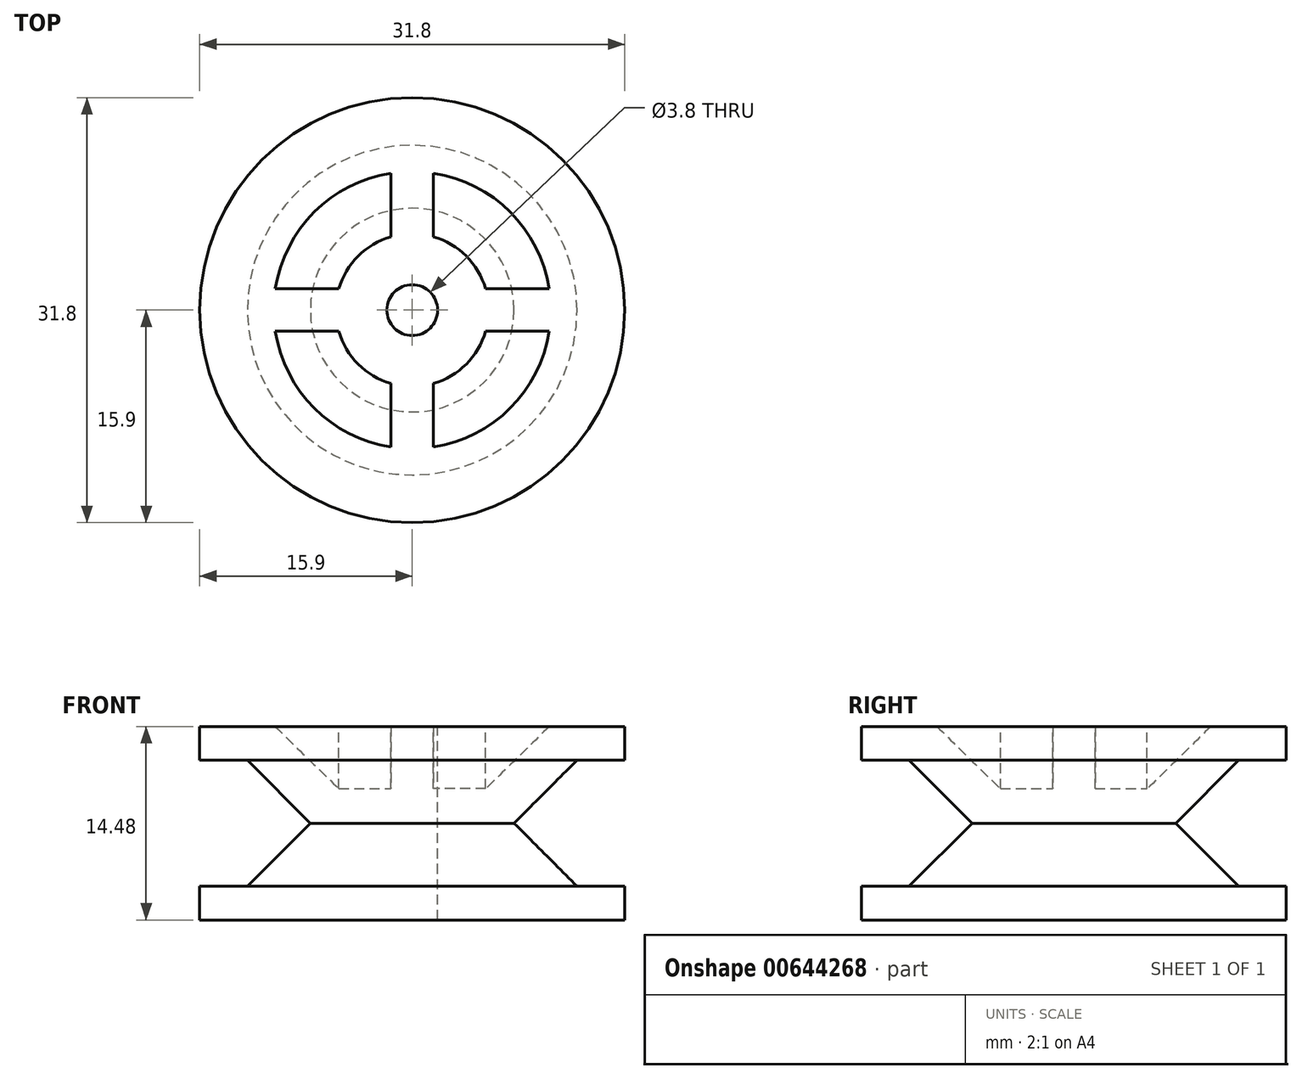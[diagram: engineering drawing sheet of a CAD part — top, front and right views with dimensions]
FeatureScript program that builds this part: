
annotation { "Feature Type Name" : "Feature", "Feature Type Description" : "" }
export const myFeature = defineFeature(function(context is Context, id is Id, definition is map)
    precondition{}
    {
        {
            var Q0;
            Q0=qCreatedBy(makeId("Top.planeOp"),FACE);
            var sketch = newSketch(context, id + "F0", { "sketchPlane" : qUnion([Q0])});
            skCircle(sketch, "E0", {"center": v(0, 0) * mm, "radius": 15.9 * mm});
            skSolve(sketch);
        }
        {
            var Q0;
            Q0 = qSketchRegion(id + "F0", true);
            extrude(context, id + "F1", {"entities" : qUnion([Q0]), "endBound" : BoundingType.SYMMETRIC, "depth" : 14.48 * mm, "offsetDistance" : 25.4 * mm});
        }
        {
            var Q0;
            Q0=makeQuery(id+"F1.opExtrude","CAP_FACE",FACE,{"disambiguationData":[OSD([sQuery(id+"F0.wireOp",EDGE,"E0")])],"isStart":false});
            var sketch = newSketch(context, id + "F2", { "sketchPlane" : qUnion([Q0])});
            skCircle(sketch, "E1", {"center": v(0, 0) * mm, "radius": 1.9 * mm});
            skSolve(sketch);
        }
        {
            var Q0;
            Q0 = qSketchRegion(id + "F2", true);
            extrude(context, id + "F3", {"entities" : qUnion([Q0]), "operationType" : NewBodyOperationType.REMOVE, "endBound" : BoundingType.THROUGH_ALL, "oppositeDirection" : true, "depth" : 25.4 * mm, "offsetDistance" : 25.4 * mm});
        }
        {
            var Q0;
            Q0=qCreatedBy(makeId("Right.planeOp"),FACE);
            var sketch = newSketch(context, id + "F4", { "sketchPlane" : qUnion([Q0])});
            skLineSegment(sketch, "E2", {"start": v(12.33, -4.71) * mm, "end": v(16.18, -4.71) * mm});
            skLineSegment(sketch, "E3", {"start": v(16.18, -4.71) * mm, "end": v(16.18, 4.71) * mm});
            skLineSegment(sketch, "E4", {"start": v(16.18, 4.71) * mm, "end": v(12.33, 4.71) * mm});
            skLineSegment(sketch, "E5", {"start": v(12.33, 4.71) * mm, "end": v(7.62, 0) * mm});
            skLineSegment(sketch, "E6", {"start": v(7.62, 0) * mm, "end": v(12.33, -4.71) * mm});
            skLineSegment(sketch, "E7", {"start": v(0, 0) * mm, "end": v(0, 12.59) * mm, "construction": true});
            skLineSegment(sketch, "E8", {"start": v(5.72, 8.58) * mm, "end": v(5.72, 2.59) * mm});
            skLineSegment(sketch, "E9", {"start": v(5.71, 8.58) * mm, "end": v(11.7, 8.58) * mm});
            skLineSegment(sketch, "E10", {"start": v(11.7, 8.58) * mm, "end": v(5.72, 2.59) * mm});
            skSolve(sketch);
        }
        {
            var Q0;
            Q0 = qSketchRegion(id + "F4", true);
            var Q1;
            Q1=sQuery(id+"F4.wireOp",EDGE,"E7");
            revolve(context, id + "F5", {"operationType" : NewBodyOperationType.REMOVE, "entities" : qUnion([Q0]), "axis" : qUnion([Q1]), "revolveType" : RevolveType.FULL, "oppositeDirection" : true});
        }
        {
            var Q0;
            {var subQ0=sQuery(id+"F0.wireOp",EDGE,"E0");Q0=makeQuery(id+"F5.boolean.opBoolean","SPLIT",FACE,{"disambiguationData":[TD([makeQuery(id+"F1.opExtrude","SWEPT_FACE",FACE,{"disambiguationData":[OSD([subQ0])]})])],"derivedFrom":makeQuery(id+"F1.opExtrude","CAP_FACE",FACE,{"disambiguationData":[OSD([subQ0])],"isStart":false})});}
            var sketch = newSketch(context, id + "F6", { "sketchPlane" : qUnion([Q0])});
            skLineSegment(sketch, "E11.bottom", {"start": v(1.59, 12.28) * mm, "end": v(-1.59, 12.28) * mm});
            skLineSegment(sketch, "E11.top", {"start": v(1.59, 4.66) * mm, "end": v(-1.59, 4.66) * mm});
            skLineSegment(sketch, "E11.left", {"start": v(1.59, 12.28) * mm, "end": v(1.59, 4.66) * mm});
            skLineSegment(sketch, "E11.right", {"start": v(-1.59, 12.28) * mm, "end": v(-1.59, 4.66) * mm});
            skPoint(sketch, "E11.middle", {"position": v(0, 8.47) * mm});
            skLineSegment(sketch, "E12.1.0", {"start": v(-12.28, -1.59) * mm, "end": v(-4.66, -1.59) * mm});
            skLineSegment(sketch, "E12.1.1", {"start": v(-12.28, 1.59) * mm, "end": v(-12.28, -1.59) * mm});
            skLineSegment(sketch, "E12.1.2", {"start": v(-12.28, 1.59) * mm, "end": v(-4.66, 1.59) * mm});
            skLineSegment(sketch, "E12.1.3", {"start": v(-4.66, 1.59) * mm, "end": v(-4.66, -1.59) * mm});
            skLineSegment(sketch, "E12.2.0", {"start": v(1.59, -12.28) * mm, "end": v(1.59, -4.66) * mm});
            skLineSegment(sketch, "E12.2.1", {"start": v(-1.59, -12.28) * mm, "end": v(1.59, -12.28) * mm});
            skLineSegment(sketch, "E12.2.2", {"start": v(-1.59, -12.28) * mm, "end": v(-1.59, -4.66) * mm});
            skLineSegment(sketch, "E12.2.3", {"start": v(-1.59, -4.66) * mm, "end": v(1.59, -4.66) * mm});
            skPoint(sketch, "E12.center", {"position": v(0, 0) * mm});
            skLineSegment(sketch, "E13.2.3.0", {"start": v(12.28, 1.59) * mm, "end": v(4.66, 1.59) * mm});
            skLineSegment(sketch, "E13.3.3.0", {"start": v(12.28, -1.59) * mm, "end": v(12.28, 1.59) * mm});
            skLineSegment(sketch, "E13.6.3.0", {"start": v(12.28, -1.59) * mm, "end": v(4.66, -1.59) * mm});
            skLineSegment(sketch, "E13.9.3.0", {"start": v(4.66, -1.59) * mm, "end": v(4.66, 1.59) * mm});
            skSolve(sketch);
        }
        {
            var Q0;
            Q0 = qSketchRegion(id + "F6", true);
            var Q1;
            Q1=makeQuery(id+"F5.boolean.opBoolean","COPY",FACE,{"derivedFrom":makeQuery(id+"F5.opRevolve","SWEPT_FACE",FACE,{"disambiguationData":[OSD([sQuery(id+"F4.wireOp",EDGE,"E10")])]})});
            extrude(context, id + "F7", {"entities" : qUnion([Q0]), "operationType" : NewBodyOperationType.ADD, "endBound" : BoundingType.UP_TO_SURFACE, "oppositeDirection" : true, "depth" : 25.4 * mm, "endBoundEntityFace" : qUnion([Q1]), "offsetDistance" : 25.4 * mm});
        }
    });
